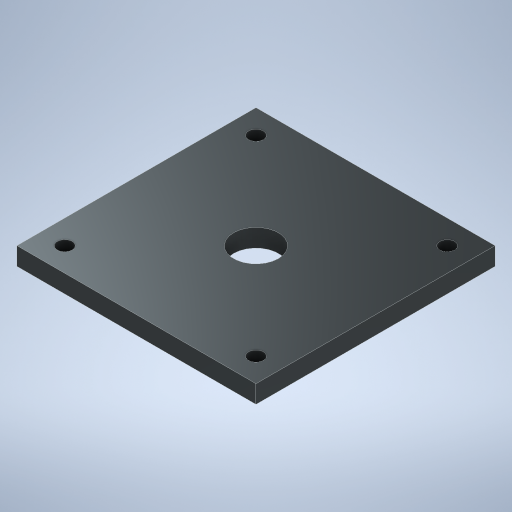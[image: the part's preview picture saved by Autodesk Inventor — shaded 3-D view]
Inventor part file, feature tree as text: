
AUTODESK INVENTOR PART (.ipt)
format: ipt  version: 2023 (Build 270158000, 158)  size: 255,488 bytes
history: native  units: mm
features: sketch x3, hole x2, other x1, extrude x1
ambient origin geometry x8: Origin, YZ Plane, XZ Plane, XY Plane, X Axis, Y Axis, Z Axis, Center Point
bodies: Body1 (feature_tree)
feature tree (7):
  other  "Sólido1"
  extrude  "Extrusão1"  Depth=80.0mm
  hole  "Furo1"  [1 undecoded]
  hole  "Furo2"  [1 undecoded]
  sketch  "Esboço1"  dims[d0=80.0mm d1=80.0mm]
  sketch  "Esboço2"  dims[d2=6.0mm d3=0.0mm d4=8.0mm]
  sketch  "Esboço3"  dims[d5=8.0mm d6=8.0mm d7=8.0mm d8=8.0mm d9=8.0mm d10=8.0mm d11=8.0mm d12=5.0mm d13=6.0mm d14=4.0mm d15=2.0mm d16=90.0deg d17=0.5mm d18=20.594885mm d19=80.0mm d20=40.0mm d21=40.0mm d22=15.0mm d23=6.0mm d24=4.0mm d25=2.0mm d26=90.0deg d27=8.0mm d28=20.594885mm]
note: 2 required parameter values undecoded (feature->parameter linkage not recoverable at this tier; creation-order binding heuristic only, values carry confidence <= 0.55)
